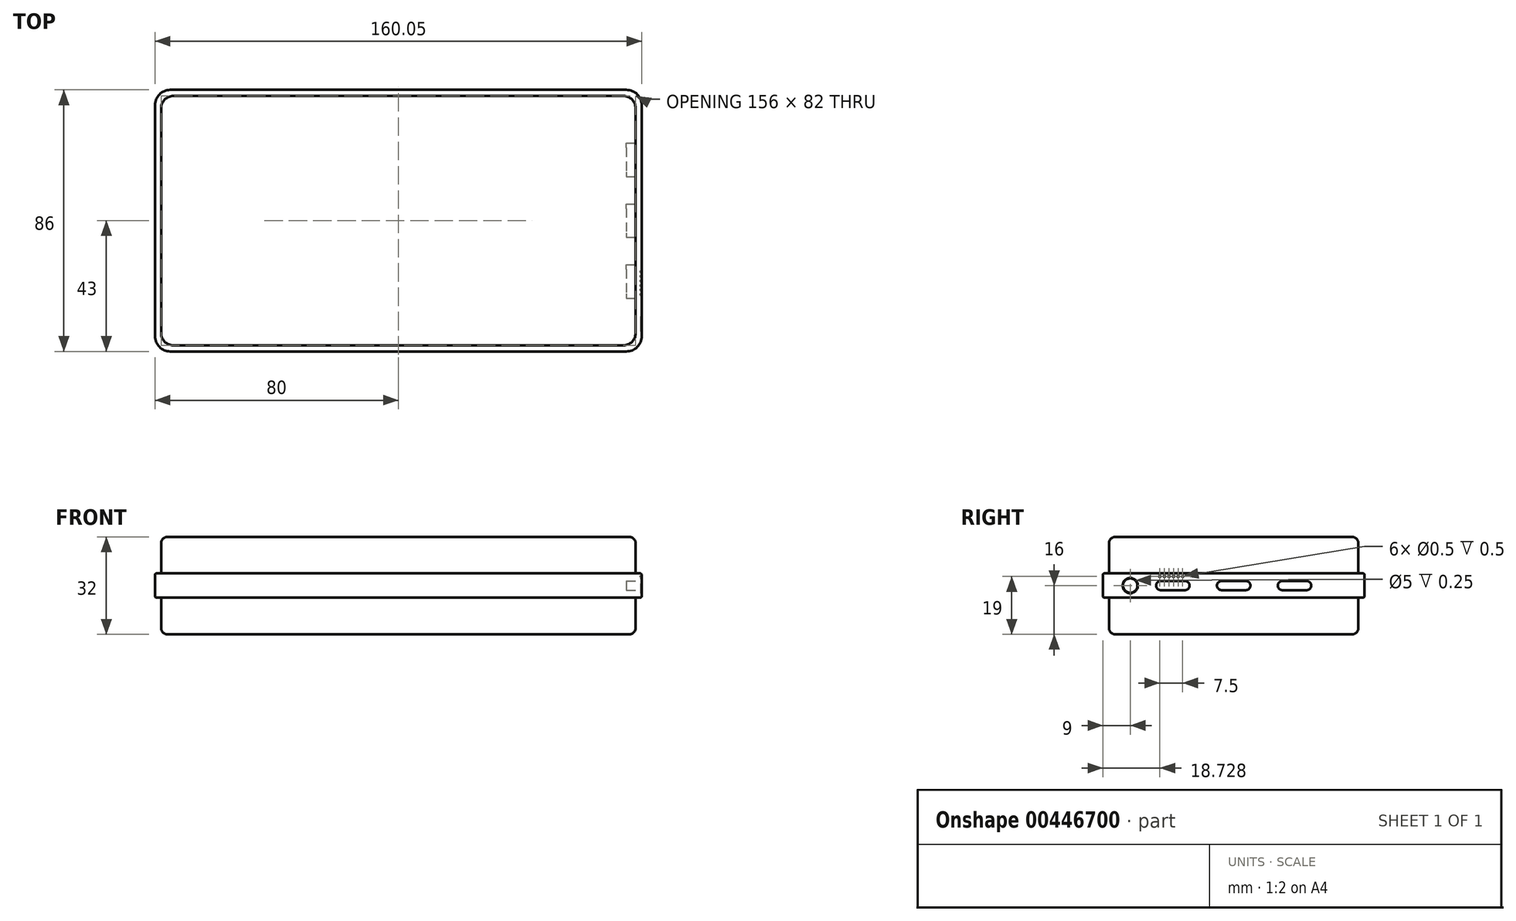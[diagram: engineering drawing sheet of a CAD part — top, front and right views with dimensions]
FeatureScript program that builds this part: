
annotation { "Feature Type Name" : "Feature", "Feature Type Description" : "" }
export const myFeature = defineFeature(function(context is Context, id is Id, definition is map)
    precondition{}
    {
        {
            var Q0;
            Q0=qCreatedBy(makeId("Top.planeOp"),FACE);
            var sketch = newSketch(context, id + "F0", { "sketchPlane" : qUnion([Q0])});
            skLineSegment(sketch, "E0.bottom", {"start": v(0, 43) * mm, "end": v(80, 43) * mm});
            skLineSegment(sketch, "E0.top", {"start": v(0, 0) * mm, "end": v(80, 0) * mm});
            skLineSegment(sketch, "E0.left", {"start": v(0, 43) * mm, "end": v(0, 0) * mm});
            skLineSegment(sketch, "E0.right", {"start": v(80, 43) * mm, "end": v(80, 0) * mm});
            skSolve(sketch);
        }
        {
            var Q0;
            Q0=makeQuery(id+"F0.imprint","IMPRINT",FACE,{"disambiguationData":[TD([[makeQuery(id+"F0.imprint","IMPRINT",EDGE,{"derivedFrom":sQuery(id+"F0.wireOp",EDGE,"E0.bottom")}),-1.0]])]});
            var Q1;
            Q1=makeQuery(id+"F0.imprint","IMPRINT",FACE,{"disambiguationData":[TD([[makeQuery(id+"F0.imprint","IMPRINT",EDGE,{"derivedFrom":sQuery(id+"F0.wireOp",EDGE,"E0.top")}),-1.0]])]});
            extrude(context, id + "F1", {"entities" : qUnion([Q0, Q1]), "depth" : 4 * mm});
        }
        {
            var Q0;
            Q0=makeQuery(id+"F1.opExtrude","CAP_FACE",FACE,{"disambiguationData":[OSD([sQuery(id+"F0.wireOp",EDGE,"E0.bottom"),sQuery(id+"F0.wireOp",EDGE,"E0.top"),sQuery(id+"F0.wireOp",EDGE,"E0.left"),sQuery(id+"F0.wireOp",EDGE,"E0.right")])],"isStart":false});
            var sketch = newSketch(context, id + "F2", { "sketchPlane" : qUnion([Q0])});
            skLineSegment(sketch, "E1.bottom", {"start": v(0, 0) * mm, "end": v(78, 0) * mm});
            skLineSegment(sketch, "E1.top", {"start": v(0, 41) * mm, "end": v(78, 41) * mm});
            skLineSegment(sketch, "E1.left", {"start": v(0, 0) * mm, "end": v(0, 41) * mm});
            skLineSegment(sketch, "E1.right", {"start": v(78, 0) * mm, "end": v(78, 41) * mm});
            skSolve(sketch);
        }
        {
            var Q0;
            Q0=makeQuery(id+"F2.imprint","IMPRINT",FACE,{"disambiguationData":[TD([[makeQuery(id+"F2.imprint","IMPRINT",EDGE,{"derivedFrom":sQuery(id+"F2.wireOp",EDGE,"E1.bottom")}),1.0]])]});
            extrude(context, id + "F3", {"entities" : qUnion([Q0]), "operationType" : NewBodyOperationType.ADD, "depth" : 12 * mm});
        }
        {
            var Q0;
            Q0=makeQuery(id+"F1.opExtrude","SWEPT_EDGE",EDGE,{"disambiguationData":[OSD([sQuery(id+"F0.wireOp",EDGE,"E0.bottom"),sQuery(id+"F0.wireOp",EDGE,"E0.right")])]});
            fillet(context, id + "F4", {"entities" : qUnion([Q0]), "radius" : 5 * mm, "tangentPropagation" : true, "allowEdgeOverflow" : false});
        }
        {
            var Q0;
            Q0=makeQuery(id+"F1.opExtrude","CAP_EDGE",EDGE,{"disambiguationData":[OSD([sQuery(id+"F0.wireOp",EDGE,"E0.bottom")])],"isStart":false});
            var Q1;
            {var subQ0=sQuery(id+"F0.wireOp",EDGE,"E0.right");var subQ1=sQuery(id+"F0.wireOp",EDGE,"E0.bottom");Q1=makeQuery(id+"F4.opFillet","BLEND_EDGE",EDGE,{"blendedFrom":[makeQuery(id+"F1.opExtrude","SWEPT_EDGE",EDGE,{"disambiguationData":[OSD([subQ1,subQ0])]}),makeQuery(id+"F1.opExtrude","CAP_FACE",FACE,{"disambiguationData":[OSD([subQ1,sQuery(id+"F0.wireOp",EDGE,"E0.top"),sQuery(id+"F0.wireOp",EDGE,"E0.left"),subQ0])],"isStart":false})],"blendedInto":[makeQuery(id+"F1.opExtrude","CAP_FACE",FACE,{"disambiguationData":[OSD([subQ1,sQuery(id+"F0.wireOp",EDGE,"E0.top"),sQuery(id+"F0.wireOp",EDGE,"E0.left"),subQ0])],"isStart":false})]});}
            var Q2;
            Q2=makeQuery(id+"F1.opExtrude","CAP_EDGE",EDGE,{"disambiguationData":[OSD([sQuery(id+"F0.wireOp",EDGE,"E0.right")])],"isStart":false});
            fillet(context, id + "F5", {"entities" : qUnion([Q0, Q1, Q2]), "radius" : 0.5 * mm, "tangentPropagation" : true, "allowEdgeOverflow" : false});
        }
        {
            var Q0;
            Q0=makeQuery(id+"F3.opExtrude","CAP_EDGE",EDGE,{"disambiguationData":[OSD([sQuery(id+"F2.wireOp",EDGE,"E1.right")])],"isStart":false});
            var Q1;
            Q1=makeQuery(id+"F3.opExtrude","CAP_EDGE",EDGE,{"disambiguationData":[OSD([sQuery(id+"F2.wireOp",EDGE,"E1.top")])],"isStart":false});
            fillet(context, id + "F6", {"entities" : qUnion([Q0, Q1]), "radius" : 2 * mm, "tangentPropagation" : true, "allowEdgeOverflow" : false});
        }
        {
            var Q0;
            Q0=makeQuery(id+"F3.opExtrude","SWEPT_EDGE",EDGE,{"disambiguationData":[OSD([sQuery(id+"F2.wireOp",EDGE,"E1.top"),sQuery(id+"F2.wireOp",EDGE,"E1.right")])]});
            fillet(context, id + "F7", {"entities" : qUnion([Q0]), "radius" : 4 * mm, "tangentPropagation" : true, "allowEdgeOverflow" : false});
        }
        {
            var Q0;
            Q0=makeQuery(id+"F1.opExtrude","SWEPT_BODY",BODY,{"disambiguationData":[OSD([sQuery(id+"F0.wireOp",EDGE,"E0.bottom"),sQuery(id+"F0.wireOp",EDGE,"E0.top"),sQuery(id+"F0.wireOp",EDGE,"E0.left"),sQuery(id+"F0.wireOp",EDGE,"E0.right")])]});
            var Q1;
            Q1=makeQuery(id+"F3.boolean.opBoolean","MERGE",FACE,{"derivedFrom":[makeQuery(id+"F1.opExtrude","SWEPT_FACE",FACE,{"disambiguationData":[OSD([sQuery(id+"F0.wireOp",EDGE,"E0.top")])]}),makeQuery(id+"F3.opExtrude","SWEPT_FACE",FACE,{"disambiguationData":[OSD([sQuery(id+"F2.wireOp",EDGE,"E1.bottom")])]})]});
            mirror(context, id + "F8", {"operationType" : NewBodyOperationType.ADD, "entities" : qUnion([Q0]), "mirrorPlane" : qUnion([Q1])});
        }
        {
            var Q0;
            Q0=makeQuery(id+"F1.opExtrude","SWEPT_BODY",BODY,{"disambiguationData":[OSD([sQuery(id+"F0.wireOp",EDGE,"E0.bottom"),sQuery(id+"F0.wireOp",EDGE,"E0.top"),sQuery(id+"F0.wireOp",EDGE,"E0.left"),sQuery(id+"F0.wireOp",EDGE,"E0.right")])]});
            var Q1;
            {var subQ0=makeQuery(id+"F3.boolean.opBoolean","MERGE",FACE,{"derivedFrom":[makeQuery(id+"F1.opExtrude","SWEPT_FACE",FACE,{"disambiguationData":[OSD([sQuery(id+"F0.wireOp",EDGE,"E0.left")])]}),makeQuery(id+"F3.opExtrude","SWEPT_FACE",FACE,{"disambiguationData":[OSD([sQuery(id+"F2.wireOp",EDGE,"E1.left")])]})]});Q1=makeQuery(id+"F8.boolean.opBoolean","MERGE",FACE,{"derivedFrom":[subQ0,makeQuery(id+"F8.opPattern","COPY",FACE,{"derivedFrom":subQ0,"instanceName":"1"})]});}
            mirror(context, id + "F9", {"operationType" : NewBodyOperationType.ADD, "entities" : qUnion([Q0]), "mirrorPlane" : qUnion([Q1])});
        }
        {
            var Q0;
            Q0=makeQuery(id+"F1.opExtrude","SWEPT_BODY",BODY,{"disambiguationData":[OSD([sQuery(id+"F0.wireOp",EDGE,"E0.bottom"),sQuery(id+"F0.wireOp",EDGE,"E0.top"),sQuery(id+"F0.wireOp",EDGE,"E0.left"),sQuery(id+"F0.wireOp",EDGE,"E0.right")])]});
            var Q1;
            {var subQ0=makeQuery(id+"F1.opExtrude","CAP_FACE",FACE,{"disambiguationData":[OSD([sQuery(id+"F0.wireOp",EDGE,"E0.bottom"),sQuery(id+"F0.wireOp",EDGE,"E0.top"),sQuery(id+"F0.wireOp",EDGE,"E0.left"),sQuery(id+"F0.wireOp",EDGE,"E0.right")])],"isStart":true});var subQ1=makeQuery(id+"F8.boolean.opBoolean","MERGE",FACE,{"derivedFrom":[subQ0,makeQuery(id+"F8.opPattern","COPY",FACE,{"derivedFrom":subQ0,"instanceName":"1"})]});Q1=makeQuery(id+"F9.boolean.opBoolean","MERGE",FACE,{"derivedFrom":[subQ1,makeQuery(id+"F9.opPattern","COPY",FACE,{"derivedFrom":subQ1,"instanceName":"1"})]});}
            mirror(context, id + "F10", {"operationType" : NewBodyOperationType.ADD, "entities" : qUnion([Q0]), "mirrorPlane" : qUnion([Q1])});
        }
        {
            var Q0;
            {var subQ0=makeQuery(id+"F1.opExtrude","SWEPT_FACE",FACE,{"disambiguationData":[OSD([sQuery(id+"F0.wireOp",EDGE,"E0.right")])]});var subQ1=makeQuery(id+"F8.boolean.opBoolean","MERGE",FACE,{"derivedFrom":[subQ0,makeQuery(id+"F8.opPattern","COPY",FACE,{"derivedFrom":subQ0,"instanceName":"1"})]});Q0=makeQuery(id+"F10.boolean.opBoolean","MERGE",FACE,{"derivedFrom":[subQ1,makeQuery(id+"F10.opPattern","COPY",FACE,{"derivedFrom":subQ1,"instanceName":"1"})]});}
            var sketch = newSketch(context, id + "F11", { "sketchPlane" : qUnion([Q0])});
            skLineSegment(sketch, "E2.bottom", {"start": v(4, -1.5) * mm, "end": v(-4, -1.5) * mm});
            skLineSegment(sketch, "E2.top", {"start": v(4, 1.5) * mm, "end": v(-4, 1.5) * mm});
            skPoint(sketch, "E2.middle", {"position": v(0, 0) * mm});
            skArc(sketch, "E3", {"start": v(-4, 1.5) * mm, "mid": v(-5.5, 0) * mm, "end": v(-4, -1.5) * mm});
            skArc(sketch, "E4", {"start": v(4, -1.5) * mm, "mid": v(5.5, 0) * mm, "end": v(4, 1.5) * mm});
            skLineSegment(sketch, "E5.bottom", {"start": v(24, -1.5) * mm, "end": v(16, -1.5) * mm});
            skLineSegment(sketch, "E5.top", {"start": v(24, 1.5) * mm, "end": v(16, 1.5) * mm});
            skArc(sketch, "E6", {"start": v(16, 1.5) * mm, "mid": v(14.5, 0) * mm, "end": v(16, -1.5) * mm});
            skArc(sketch, "E7", {"start": v(24, -1.5) * mm, "mid": v(25.5, 0) * mm, "end": v(24, 1.5) * mm});
            skLineSegment(sketch, "E8.bottom", {"start": v(-16, -1.5) * mm, "end": v(-24, -1.5) * mm});
            skLineSegment(sketch, "E8.top", {"start": v(-16, 1.5) * mm, "end": v(-24, 1.5) * mm});
            skArc(sketch, "E9", {"start": v(-24, 1.5) * mm, "mid": v(-25.5, 0) * mm, "end": v(-24, -1.5) * mm});
            skArc(sketch, "E10", {"start": v(-16, -1.5) * mm, "mid": v(-14.5, 0) * mm, "end": v(-16, 1.5) * mm});
            skCircle(sketch, "E11", {"center": v(-34, 0) * mm, "radius": 2.5 * mm});
            skSolve(sketch);
        }
        {
            var Q0;
            Q0=makeQuery(id+"F11.imprint","IMPRINT",FACE,{"disambiguationData":[TD([[makeQuery(id+"F11.imprint","IMPRINT",EDGE,{"derivedFrom":sQuery(id+"F11.wireOp",EDGE,"E11")}),1.0]])]});
            extrude(context, id + "F12", {"entities" : qUnion([Q0]), "operationType" : NewBodyOperationType.REMOVE, "oppositeDirection" : true, "depth" : 0.25 * mm});
        }
        {
            var Q0;
            Q0=makeQuery(id+"F11.imprint","IMPRINT",FACE,{"disambiguationData":[TD([[makeQuery(id+"F11.imprint","IMPRINT",EDGE,{"derivedFrom":sQuery(id+"F11.wireOp",EDGE,"E8.bottom")}),-1.0]])]});
            var Q1;
            Q1=makeQuery(id+"F11.imprint","IMPRINT",FACE,{"disambiguationData":[TD([[makeQuery(id+"F11.imprint","IMPRINT",EDGE,{"derivedFrom":sQuery(id+"F11.wireOp",EDGE,"E2.bottom")}),-1.0]])]});
            var Q2;
            Q2=makeQuery(id+"F11.imprint","IMPRINT",FACE,{"disambiguationData":[TD([[makeQuery(id+"F11.imprint","IMPRINT",EDGE,{"derivedFrom":sQuery(id+"F11.wireOp",EDGE,"E5.bottom")}),-1.0]])]});
            extrude(context, id + "F13", {"entities" : qUnion([Q0, Q1, Q2]), "operationType" : NewBodyOperationType.REMOVE, "oppositeDirection" : true, "depth" : 5 * mm});
        }
        {
            var Q0;
            Q0=makeQuery(id+"F12.boolean.opBoolean","COPY",FACE,{"derivedFrom":makeQuery(id+"F12.opExtrude","CAP_FACE",FACE,{"disambiguationData":[OSD([sQuery(id+"F11.wireOp",EDGE,"E11")])],"isStart":false})});
            var sketch = newSketch(context, id + "F14", { "sketchPlane" : qUnion([Q0])});
            skCircle(sketch, "E12", {"center": v(-34, 0) * mm, "radius": 2.38 * mm});
            skSolve(sketch);
        }
        {
            var Q0;
            Q0=makeQuery(id+"F14.imprint","IMPRINT",FACE,{"disambiguationData":[TD([[makeQuery(id+"F14.imprint","IMPRINT",EDGE,{"derivedFrom":sQuery(id+"F14.wireOp",EDGE,"E12")}),1.0]])]});
            extrude(context, id + "F15", {"entities" : qUnion([Q0]), "operationType" : NewBodyOperationType.ADD, "depth" : 0.3 * mm});
        }
        {
            var Q0;
            {var subQ0=makeQuery(id+"F1.opExtrude","SWEPT_FACE",FACE,{"disambiguationData":[OSD([sQuery(id+"F0.wireOp",EDGE,"E0.right")])]});var subQ1=makeQuery(id+"F8.boolean.opBoolean","MERGE",FACE,{"derivedFrom":[subQ0,makeQuery(id+"F8.opPattern","COPY",FACE,{"derivedFrom":subQ0,"instanceName":"1"})]});Q0=makeQuery(id+"F10.boolean.opBoolean","MERGE",FACE,{"derivedFrom":[subQ1,makeQuery(id+"F10.opPattern","COPY",FACE,{"derivedFrom":subQ1,"instanceName":"1"})]});}
            var sketch = newSketch(context, id + "F16", { "sketchPlane" : qUnion([Q0])});
            skCircle(sketch, "E13", {"center": v(-21.27, 3) * mm, "radius": 0.25 * mm});
            skCircle(sketch, "E14", {"center": v(-18.27, 3) * mm, "radius": 0.25 * mm});
            skCircle(sketch, "E15", {"center": v(-16.77, 3) * mm, "radius": 0.25 * mm});
            skCircle(sketch, "E16", {"center": v(-22.77, 3) * mm, "radius": 0.25 * mm});
            skCircle(sketch, "E17", {"center": v(-24.27, 3) * mm, "radius": 0.25 * mm});
            skCircle(sketch, "E18", {"center": v(-19.77, 3) * mm, "radius": 0.25 * mm});
            skSolve(sketch);
        }
        {
            var Q0;
            Q0 = qSketchRegion(id + "F16", true);
            extrude(context, id + "F17", {"entities" : qUnion([Q0]), "operationType" : NewBodyOperationType.REMOVE, "oppositeDirection" : true, "depth" : 0.5 * mm});
        }
    });
